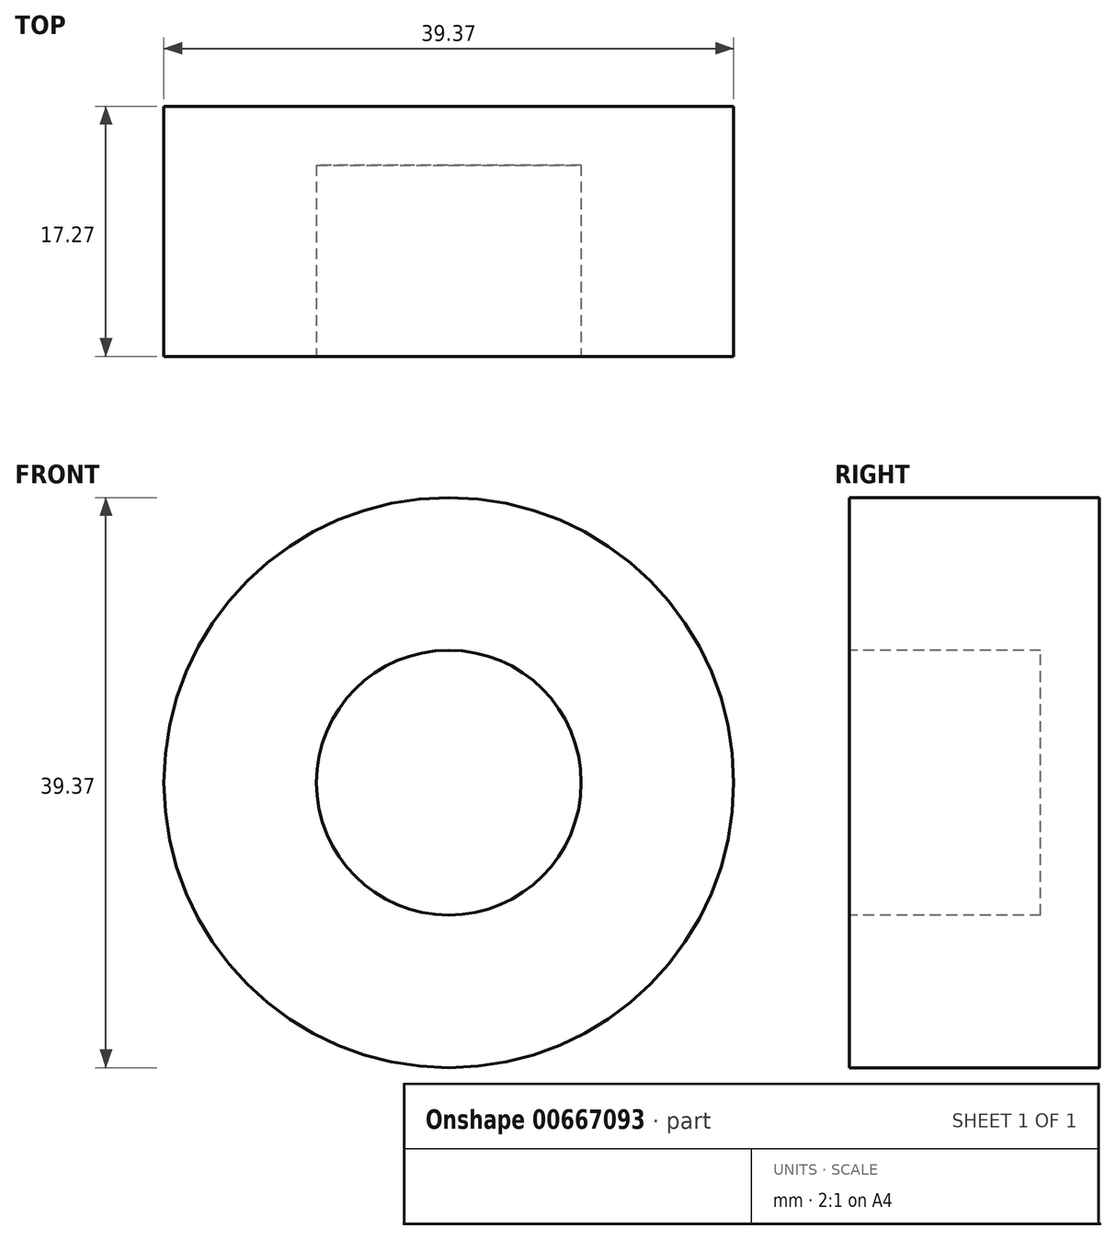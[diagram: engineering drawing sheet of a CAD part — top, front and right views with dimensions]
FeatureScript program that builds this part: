
annotation { "Feature Type Name" : "Feature", "Feature Type Description" : "" }
export const myFeature = defineFeature(function(context is Context, id is Id, definition is map)
    precondition{}
    {
        {
            var Q0;
            Q0=qCreatedBy(makeId("Front.planeOp"),FACE);
            var sketch = newSketch(context, id + "F0", { "sketchPlane" : qUnion([Q0])});
            skCircle(sketch, "E0", {"center": v(291.7, 104.72) * mm, "radius": 19.69 * mm});
            skSolve(sketch);
        }
        {
            var Q0;
            Q0 = qSketchRegion(id + "F0", true);
            extrude(context, id + "F1", {"entities" : qUnion([Q0]), "depth" : 17.27 * mm, "offsetDistance" : 25.4 * mm});
        }
        {
            var Q0;
            Q0=makeQuery(id+"F1.opExtrude","CAP_FACE",FACE,{"disambiguationData":[OSD([sQuery(id+"F0.wireOp",EDGE,"E0")])],"isStart":false});
            var sketch = newSketch(context, id + "F2", { "sketchPlane" : qUnion([Q0])});
            skCircle(sketch, "E1.0.0", {"center": v(291.7, 104.72) * mm, "radius": 19.69 * mm});
            skCircle(sketch, "E2", {"center": v(291.7, 104.72) * mm, "radius": 9.14 * mm});
            skSolve(sketch);
        }
        {
            var Q0;
            Q0=makeQuery(id+"F2.imprint","IMPRINT",FACE,{"disambiguationData":[TD([[makeQuery(id+"F2.imprint","IMPRINT",EDGE,{"derivedFrom":sQuery(id+"F2.wireOp",EDGE,"E2")}),1.0]])]});
            var sketch = newSketch(context, id + "F3", { "sketchPlane" : qUnion([Q0])});
            skSolve(sketch);
        }
        {
            var Q0;
            Q0=makeQuery(id+"F3.imprint","IMPRINT",FACE,{"disambiguationData":[TD([[makeQuery(id+"F3.imprint","IMPRINT",EDGE,{"derivedFrom":makeQuery(id+"F2.imprint","IMPRINT",EDGE,{"derivedFrom":sQuery(id+"F2.wireOp",EDGE,"E2")})}),1.0]])]});
            var sketch = newSketch(context, id + "F4", { "sketchPlane" : qUnion([Q0])});
            skSolve(sketch);
        }
        {
            var Q0;
            Q0=makeQuery(id+"F3.imprint","IMPRINT",FACE,{"disambiguationData":[TD([[makeQuery(id+"F3.imprint","IMPRINT",EDGE,{"derivedFrom":makeQuery(id+"F2.imprint","IMPRINT",EDGE,{"derivedFrom":sQuery(id+"F2.wireOp",EDGE,"E2")})}),1.0]])]});
            extrude(context, id + "F5", {"entities" : qUnion([Q0]), "operationType" : NewBodyOperationType.REMOVE, "oppositeDirection" : true, "depth" : 13.2 * mm, "offsetDistance" : 25.4 * mm});
        }
        {
            var Q0;
            Q0=makeQuery(id+"F1.opExtrude","SWEPT_BODY",BODY,{"disambiguationData":[OSD([sQuery(id+"F0.wireOp",EDGE,"E0")])]});
            transform(context, id + "F6", {"entities" : qUnion([Q0]), "transformType" : TransformType.TRANSLATION_3D, "dx" : 0 * mm, "dy" : 0 * mm, "dz" : 0 * mm, "makeCopy" : true});
        }
    });
